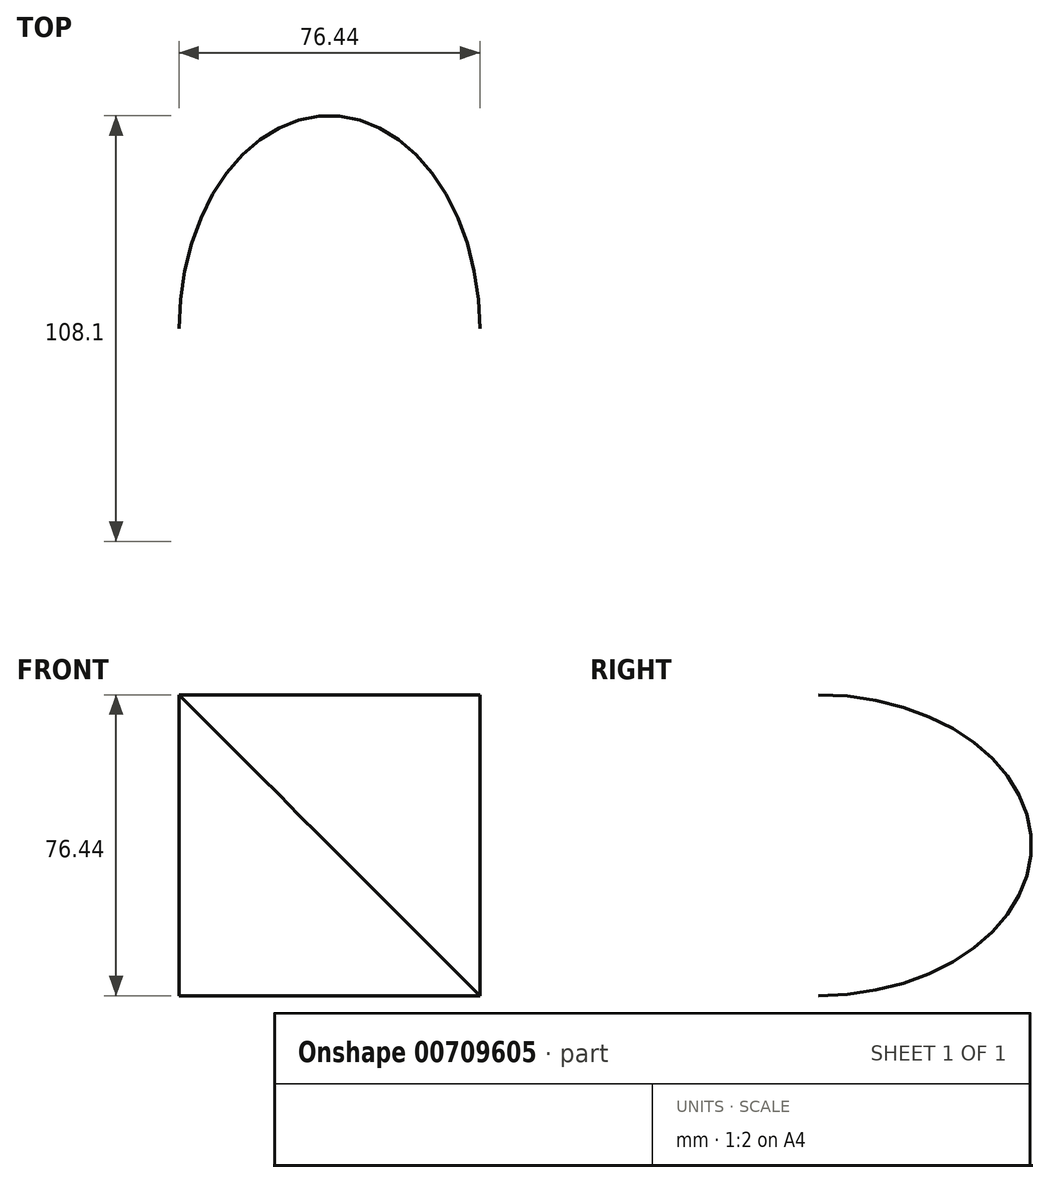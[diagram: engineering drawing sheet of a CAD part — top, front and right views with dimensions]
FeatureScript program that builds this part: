
annotation { "Feature Type Name" : "Feature", "Feature Type Description" : "" }
export const myFeature = defineFeature(function(context is Context, id is Id, definition is map)
    precondition{}
    {
        {
            var Q0;
            Q0=qCreatedBy(makeId("Front.planeOp"),FACE);
            var sketch = newSketch(context, id + "F0", { "sketchPlane" : qUnion([Q0])});
            skLineSegment(sketch, "E0.bottom", {"start": v(0, 0) * mm, "end": v(-76.44, 0) * mm});
            skLineSegment(sketch, "E0.top", {"start": v(0, 76.44) * mm, "end": v(-76.44, 76.44) * mm});
            skLineSegment(sketch, "E0.left", {"start": v(0, 0) * mm, "end": v(0, 76.44) * mm});
            skLineSegment(sketch, "E0.right", {"start": v(-76.44, 0) * mm, "end": v(-76.44, 76.44) * mm});
            skLineSegment(sketch, "E1", {"start": v(-76.44, 0) * mm, "end": v(0, 76.44) * mm});
            skSolve(sketch);
        }
        {
            var Q0;
            Q0=makeQuery(id+"F0.imprint","IMPRINT",FACE,{"disambiguationData":[TD([[makeQuery(id+"F0.imprint","IMPRINT",EDGE,{"derivedFrom":sQuery(id+"F0.wireOp",EDGE,"E0.top")}),1.0]])]});
            var Q1;
            Q1=sQuery(id+"F0.wireOp",EDGE,"E1");
            revolve(context, id + "F1", {"surfaceOperationType" : NewSurfaceOperationType.NEW, "entities" : qUnion([Q0]), "axis" : qUnion([Q1]), "revolveType" : RevolveType.FULL});
        }
    });
